# Revit family: サイド実験台 H800xW1800xD750 Assy フラットタイプ_Shrinkwrap_2
name_source: partatom
category: Generic Models
units: mm (PartAtom-declared; Revit-internal decimal feet)

## family parameters
Always vertical = Yes
Can host rebar = No
Cut with Voids When Loaded = No
Part Type = Normal
Room Calculation Point = No
Round Connector Dimension = Use Diameter
Shared = No
Work Plane-Based = No

## types (1)
- Standard
    Default Elevation = 0 mm  [stored 0 ft]
    Manufacturer = 三進金属工業株式会社
    URL = https://www.sanshinkinzoku.co.jp
    タイプ = フラットタイプ
    品名 = ワイドフリーベンチ
    品番 = WSB-1875-STTF
    天板 = BF 天板（スリムタイプ）
    天板耐荷重 = 500kg/ スパン（等分布載荷）
    奥行-D = 750 mm  [stored 2.46063 ft]
    本体材質 = スチール製（粉体塗装仕上げ）
    本体標準色 = マイルドホワイト
    質量 = 118kg
    間口-W = 1800 mm  [stored 5.90551 ft]
    高さ-H = 800 mm  [stored 2.62467 ft]

note: [stored X ft] marks values corroborated as IEEE doubles in the binary element streams (Revit-internal decimal feet)

## geometry (parser evidence)
native form markers: Sweep x3
no freeform markers — native parametric forms only
